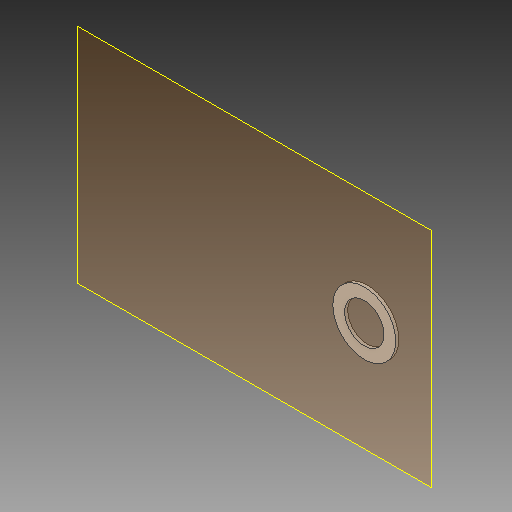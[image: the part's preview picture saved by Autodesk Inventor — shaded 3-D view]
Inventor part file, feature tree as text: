
AUTODESK INVENTOR PART (.ipt)
format: ipt  version: 2017 (Build 210142000, 142)  size: 84,992 bytes
history: native  units: mm
features: other x3, sketch x1, plane x1
ambient origin geometry x8: Origin, YZ Plane, XZ Plane, XY Plane, X Axis, Y Axis, Z Axis, Center Point
bodies: Solid1 (feature_tree)
feature tree (5):
  other  "Washer.ipt"
  other  "Solid1::Washer.ipt"
  other  "TaggingFeature1"
  sketch  "Sketch1"  dims[d0=10.0mm]
  plane  "Work Plane1"
